# Revit family: Haworth_Nia_Chair_AP_PRELIMINARY
name_source: partatom
category: Furniture
units: mm (PartAtom-declared; Revit-internal decimal feet)

## family parameters
Always vertical = Yes
Cut with Voids When Loaded = No
OmniClass Number = 23.40.20.00
OmniClass Title = General Furniture and Specialties
Room Calculation Point = No
Shared = No
Work Plane-Based = No

## types (6) — shared parameters
Actual Depth = 680 mm  [stored 2.23097 ft]
Actual Width = 680 mm  [stored 2.23097 ft]
Assembly Code = E2020200
Caster Finish = Haworth _ Polymer _ Black
Description = Haworth - Nia - Chair - Task
Hardware Finish = Haworth _ Paint _ Black
Manufacturer = Haworth
Model = SENIAX
Plastic Trim Finish = Haworth _ Polymer _ Black
Size = Verify Final Dim. w/ Haworth
URL = https://www.haworth.com
URL - Product = https://www.haworth.com
Version = 1
Warranty = http://www.haworth.com

## per-type parameters (varying)
| type | Actual Height | Fixed Arms | Height Adjustable Arms | High Back | Mid Back | Seat Height | Stool Chair | Task Chair | With Arms | Without Arms |
| High Back - Fixed Arms | 1070 mm  [stored 3.5105 ft] | Yes | No | Yes | No | 180 mm  [stored 0.590551 ft] | Yes | No | Yes | No |
| High Back - Without Arms | 1070 mm  [stored 3.5105 ft] | No | No | Yes | No | 0 mm  [stored 0 ft] | No | Yes | No | Yes |
| Mid Back - Fixed Arms | 1010 mm  [stored 3.31365 ft] | Yes | No | No | Yes | 0 mm  [stored 0 ft] | No | Yes | Yes | No |
| Mid Back - Without Arms | 1010 mm  [stored 3.31365 ft] | No | No | No | Yes | 0 mm  [stored 0 ft] | No | Yes | No | Yes |
| High Back - Height Adjustable Arms | 1070 mm  [stored 3.5105 ft] | No | Yes | Yes | No | 180 mm  [stored 0.590551 ft] | Yes | No | Yes | No |
| Mid Back - Height Adjustable Arms | 1010 mm  [stored 3.31365 ft] | No | Yes | No | Yes | 0 mm  [stored 0 ft] | No | Yes | Yes | No |

note: [stored X ft] marks values corroborated as IEEE doubles in the binary element streams (Revit-internal decimal feet)

## geometry (parser evidence)
native form markers: Sweep x16
no freeform markers — native parametric forms only
